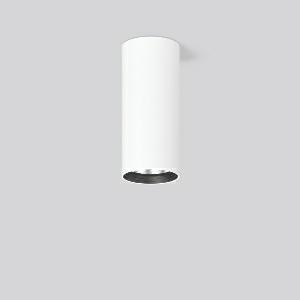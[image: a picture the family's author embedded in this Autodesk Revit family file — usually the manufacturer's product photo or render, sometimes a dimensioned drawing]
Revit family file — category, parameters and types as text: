
# Revit family: heledon_mini_a_931208_002_76_01ce
name_source: partatom
category: Lighting Fixtures
units: mm (PartAtom-declared; Revit-internal decimal feet)

## family parameters
Cut with Voids When Loaded = No
Host = Face
Light Source = No
Part Type = Normal
Room Calculation Point = No
Round Connector Dimension = Use Diameter
Shared = No

## types (1)
- HELEDON mini A (1 x LED Modul 930, 3550 lm, 3000)
    Apparent Load = 29 VA
    Approval mark = CE
    CIE Flux Codes = 100 100 100 100 100
    Color Rendering = 90
    Color Temperature = 3000
    Default Elevation = 1800 mm
    Description = Series: HELEDON mini
Cylindrical surface-mounted downlight. Housing: die-cast aluminium, powder-coated. Internal ceiling frame polycarbonate with bayonet mounting. Black plastic ring and recessed LED to prevent glare from the side. Optical assembly with reflector made of MIRO-Silver with 98% total light reflection for outstanding efficiency - can be changed without tools. Best colour rendering index Ra>90. Suitable for Ceiling mounting. Easy installation with a separate ceiling frame with bayonet mounting and plug connection. Driver integrated. Connected via plug-in connector. High quality converter without flickering and stroboscopic effect. The following accessories can be mounted without use of tools: interchangeable lenses, decorative glasses, honeycomb louvre, clear and frosted diffusers, white interchangeable plastic ring. 
Colour: traffic white, matt (RAL 9016)
Diameter: 87 mm
Height: 197 mm
Lamp: LED
Socket: without socket
Colour temperature: 3000K
Colour rendering index (CRI): 92
System power: 29 W
Rated luminous flux: 3550 lm
Luminous efficiency: 122 lm/W
Control gear: Converter, dimmable, DALI
Protection class: I
Type of protection: IP 20
    Height = 197 mm
    Lamp = 1 x LED Modul 930
    Lamp Light Flux = 3550 lm
    Lamp count = 1
    Length = 87 mm
    Lifetime = 50000 h
    Luminous efficacy = 122 lm/W
    Manufacturer = RZB
    ModVariant = No
    Model = 931208.002.76
    Mounting Place = Ceiling
    Mounting Type = Surface mounted
    Number of Poles = 1
    OnlyDefault = Yes
    Power Factor = 1
    Product Name = HELEDON mini A
    Product group = Surface mounted downlights
    ProductGroupID = 302
    Protection Class = Protection class I
    Protection Degree = IP 20
    RLX_Detail_Level = 1
    RLX_Emergency_Light_Flux = 0 lm
    RLX_Emergency_Type = 0
    RLX_Emergency_Type_DB = No
    RlxData = <blob elided: 107289 chars, md5=3033d828>
    Socket = socket
    Standby Power = 0 W
    System Light Flux = 3550 lm
    System Power = 29 W
    Type Comments = Product without accessories
    Type Image = 931188.002.jpg
    URL = http://relux.com
    VarID = ---
    Voltage = 230 V
    Voltage Range = 220-240 V
    Weight = 0.00 kg
    Width = 0 mm  [stored 0 ft]

note: [stored X ft] marks values corroborated as IEEE doubles in the binary element streams (Revit-internal decimal feet)

## geometry (parser evidence)
native form markers: Blend x4, Sweep x10
no freeform markers — native parametric forms only
